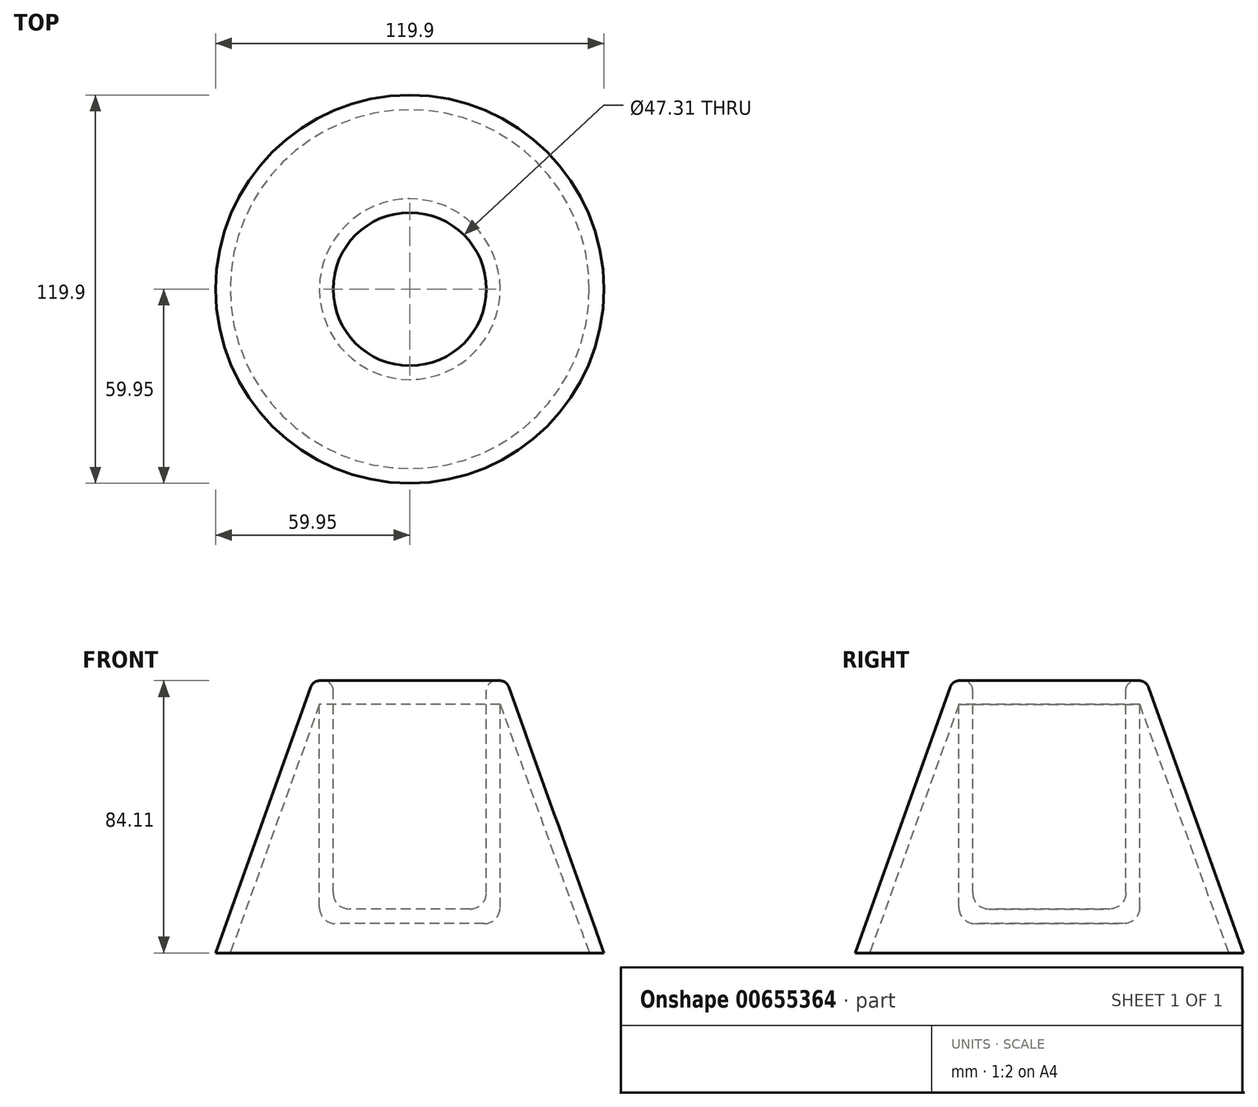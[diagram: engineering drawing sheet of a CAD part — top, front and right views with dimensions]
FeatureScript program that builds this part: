
annotation { "Feature Type Name" : "Feature", "Feature Type Description" : "" }
export const myFeature = defineFeature(function(context is Context, id is Id, definition is map)
    precondition{}
    {
        {
            var Q0;
            Q0=qCreatedBy(makeId("Front.planeOp"),FACE);
            var sketch = newSketch(context, id + "F0", { "sketchPlane" : qUnion([Q0])});
            skLineSegment(sketch, "E0", {"start": v(0, -27.62) * mm, "end": v(-23.65, -27.62) * mm});
            skLineSegment(sketch, "E1", {"start": v(0, -32.15) * mm, "end": v(-23.37, -32.15) * mm});
            skLineSegment(sketch, "E2", {"start": v(-23.65, -27.62) * mm, "end": v(-23.65, 42.92) * mm});
            skLineSegment(sketch, "E3", {"start": v(-23.65, 42.92) * mm, "end": v(-29.89, 42.92) * mm});
            skLineSegment(sketch, "E4", {"start": v(-29.89, 42.92) * mm, "end": v(-59.95, -41.2) * mm});
            skLineSegment(sketch, "E5", {"start": v(-23.37, -32.15) * mm, "end": v(-27.9, -32.15) * mm});
            skLineSegment(sketch, "E6", {"start": v(-27.9, -32.15) * mm, "end": v(-27.9, 35.55) * mm});
            skLineSegment(sketch, "E7", {"start": v(-27.9, 35.55) * mm, "end": v(-55.43, -41.2) * mm});
            skLineSegment(sketch, "E8", {"start": v(0, -27.62) * mm, "end": v(0, -32.15) * mm});
            skLineSegment(sketch, "E9", {"start": v(-55.43, -41.2) * mm, "end": v(-59.95, -41.2) * mm});
            skPoint(sketch, "E10.end.orphan", {"position": v(-50.56, -27.62) * mm});
            skPoint(sketch, "E10.start.orphan", {"position": v(-55.1, -27.62) * mm});
            skSolve(sketch);
        }
        {
            var Q0;
            Q0 = qSketchRegion(id + "F0", true);
            var Q1;
            Q1=sQuery(id+"F0.wireOp",EDGE,"E8");
            revolve(context, id + "F1", {"entities" : qUnion([Q0]), "axis" : qUnion([Q1]), "revolveType" : RevolveType.FULL});
        }
        {
            var Q0;
            Q0=makeQuery(id+"F1.opRevolve","SWEPT_EDGE",EDGE,{"disambiguationData":[OSD([sQuery(id+"F0.wireOp",EDGE,"E3"),sQuery(id+"F0.wireOp",EDGE,"E4")])]});
            var Q1;
            Q1=makeQuery(id+"F1.opRevolve","SWEPT_EDGE",EDGE,{"disambiguationData":[OSD([sQuery(id+"F0.wireOp",EDGE,"E2"),sQuery(id+"F0.wireOp",EDGE,"E3")])]});
            fillet(context, id + "F2", {"entities" : qUnion([Q0, Q1]), "radius" : 3 * mm, "tangentPropagation" : true, "allowEdgeOverflow" : false});
        }
        {
            var Q0;
            Q0=makeQuery(id+"F1.opRevolve","SWEPT_EDGE",EDGE,{"disambiguationData":[OSD([sQuery(id+"F0.wireOp",EDGE,"E0"),sQuery(id+"F0.wireOp",EDGE,"E2")])]});
            fillet(context, id + "F3", {"entities" : qUnion([Q0]), "radius" : 5 * mm, "tangentPropagation" : true, "allowEdgeOverflow" : false});
        }
        {
            var Q0;
            Q0=makeQuery(id+"F1.opRevolve","SWEPT_EDGE",EDGE,{"disambiguationData":[OSD([sQuery(id+"F0.wireOp",EDGE,"E5"),sQuery(id+"F0.wireOp",EDGE,"E6")])]});
            fillet(context, id + "F4", {"entities" : qUnion([Q0]), "radius" : 5 * mm, "tangentPropagation" : true, "allowEdgeOverflow" : false});
        }
    });
